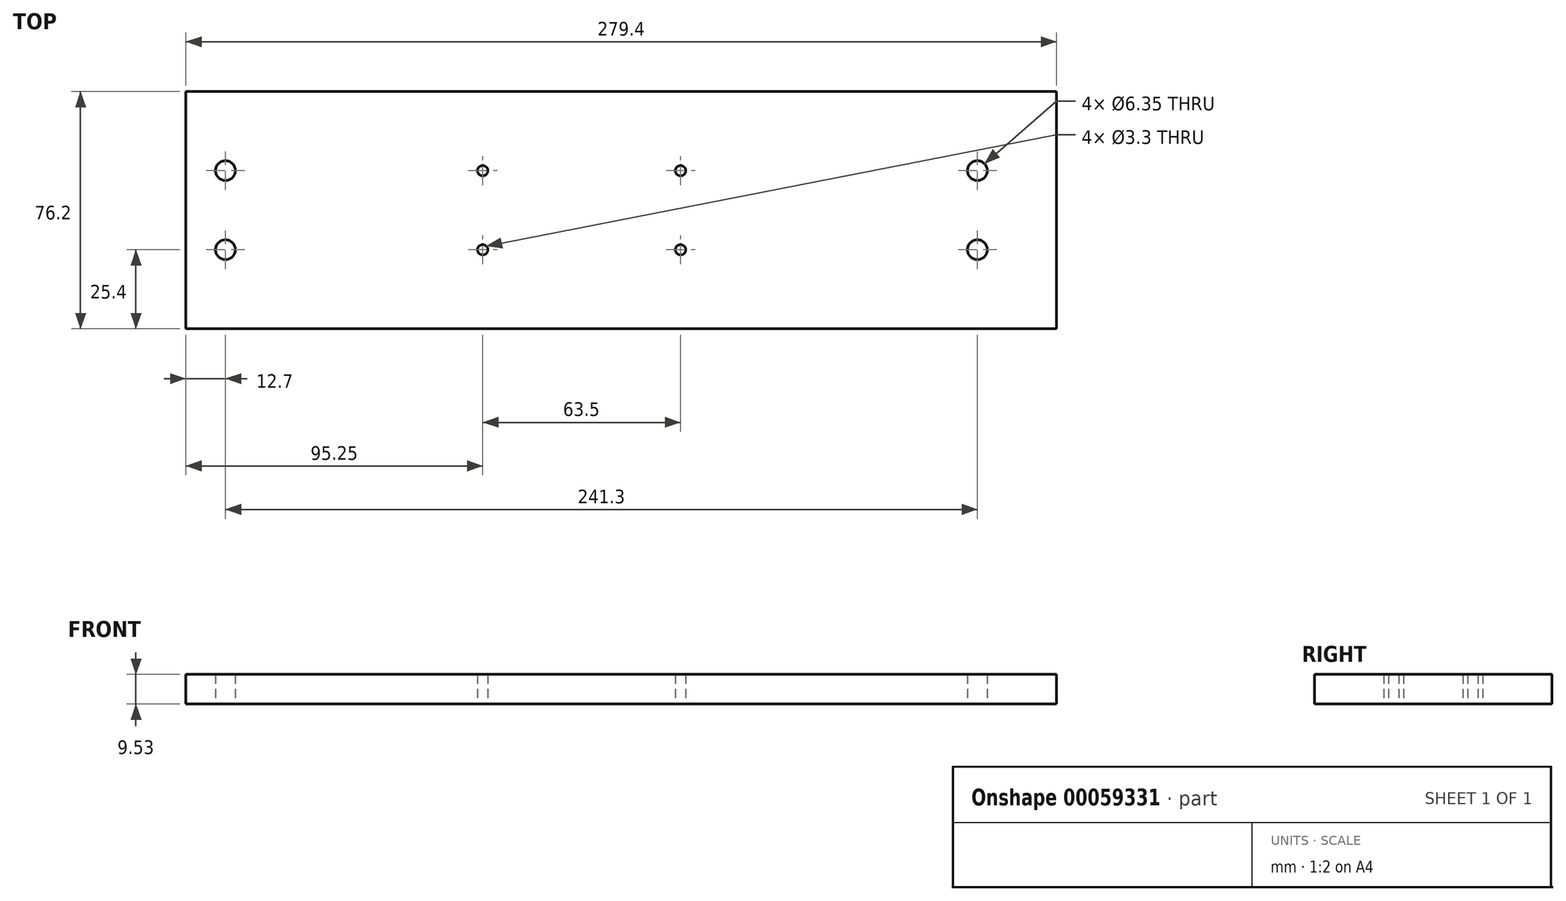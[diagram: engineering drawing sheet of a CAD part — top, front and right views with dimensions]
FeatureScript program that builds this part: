
annotation { "Feature Type Name" : "Feature", "Feature Type Description" : "" }
export const myFeature = defineFeature(function(context is Context, id is Id, definition is map)
    precondition{}
    {
        {
            var Q0;
            Q0=qCreatedBy(makeId("Top.planeOp"),FACE);
            var sketch = newSketch(context, id + "F0", { "sketchPlane" : qUnion([Q0])});
            skLineSegment(sketch, "E0.bottom", {"start": v(0, 0) * mm, "end": v(279.4, 0) * mm});
            skLineSegment(sketch, "E0.top", {"start": v(0, -76.2) * mm, "end": v(279.4, -76.2) * mm});
            skLineSegment(sketch, "E0.left", {"start": v(0, 0) * mm, "end": v(0, -76.2) * mm});
            skLineSegment(sketch, "E0.right", {"start": v(279.4, 0) * mm, "end": v(279.4, -76.2) * mm});
            skLineSegment(sketch, "E1", {"start": v(-11.39, -38.1) * mm, "end": v(294.56, -38.1) * mm, "construction": true});
            skPoint(sketch, "E1.startSnap0", {"position": v(0, -38.1) * mm});
            skPoint(sketch, "E1.endSnap0", {"position": v(279.4, -38.1) * mm});
            skCircle(sketch, "E2", {"center": v(12.7, -25.4) * mm, "radius": 3.18 * mm});
            skCircle(sketch, "E3", {"center": v(12.7, -50.8) * mm, "radius": 3.18 * mm});
            skCircle(sketch, "E4", {"center": v(95.25, -25.4) * mm, "radius": 1.65 * mm});
            skCircle(sketch, "E5", {"center": v(95.25, -50.8) * mm, "radius": 1.65 * mm});
            skCircle(sketch, "E6", {"center": v(158.75, -25.4) * mm, "radius": 1.65 * mm});
            skCircle(sketch, "E7", {"center": v(158.75, -50.8) * mm, "radius": 1.65 * mm});
            skCircle(sketch, "E8", {"center": v(254, -25.4) * mm, "radius": 3.18 * mm});
            skCircle(sketch, "E9", {"center": v(254, -50.8) * mm, "radius": 3.18 * mm});
            skSolve(sketch);
        }
        {
            var Q0;
            Q0 = qSketchRegion(id + "F0", true);
            extrude(context, id + "F1", {"entities" : qUnion([Q0]), "depth" : 9.52 * mm});
        }
    });
